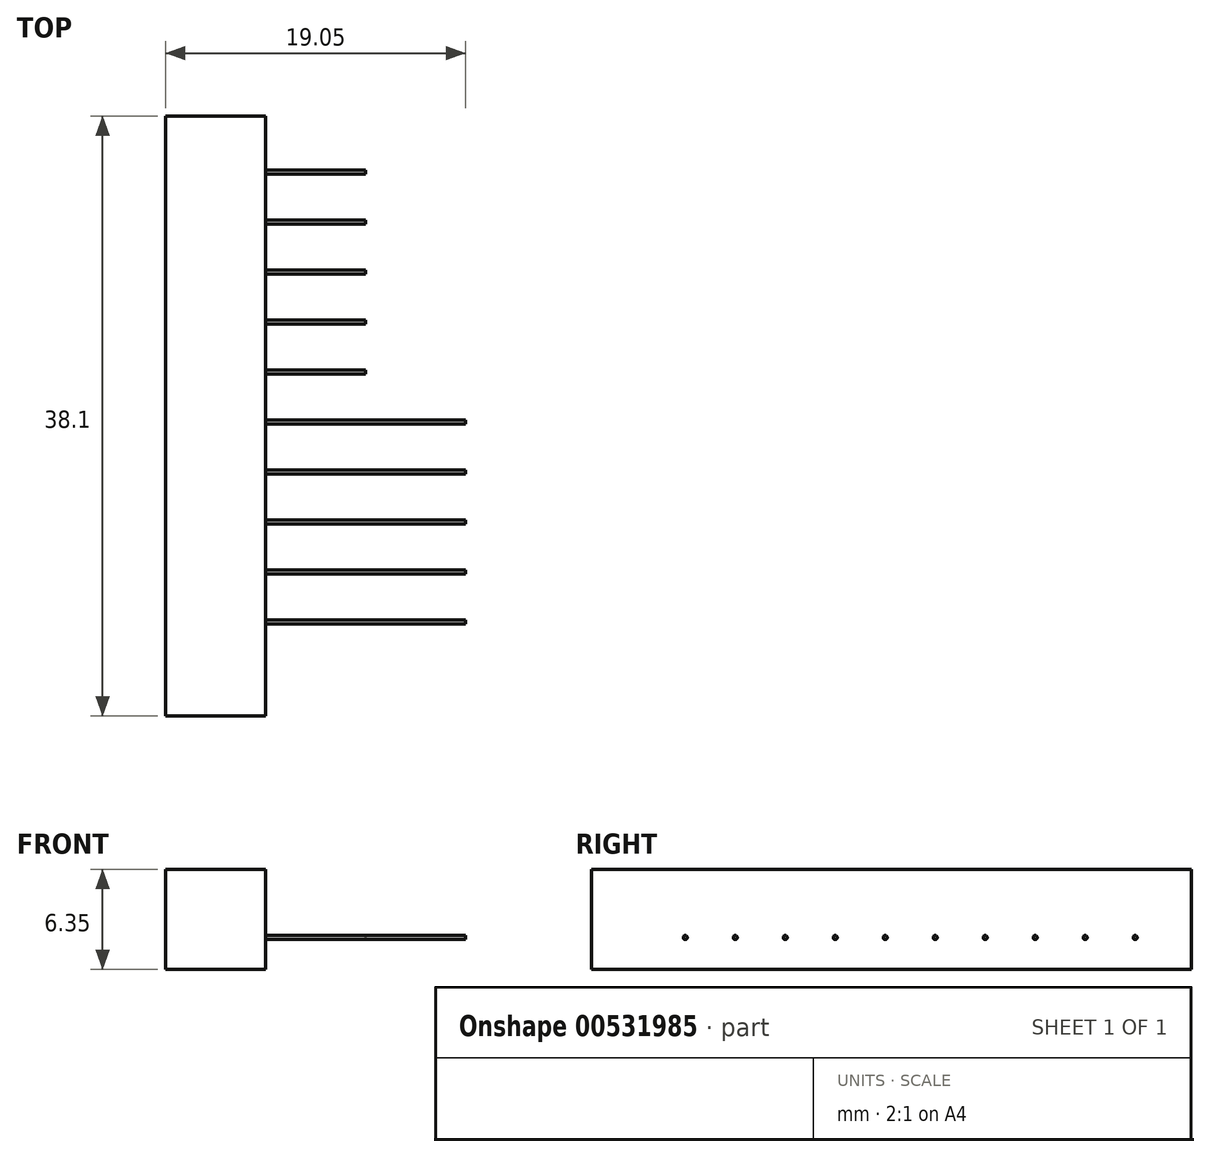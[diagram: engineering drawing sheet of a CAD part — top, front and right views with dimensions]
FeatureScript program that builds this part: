
annotation { "Feature Type Name" : "Feature", "Feature Type Description" : "" }
export const myFeature = defineFeature(function(context is Context, id is Id, definition is map)
    precondition{}
    {
        {
            var Q0;
            Q0=qCreatedBy(makeId("Top.planeOp"),FACE);
            var sketch = newSketch(context, id + "F0", { "sketchPlane" : qUnion([Q0])});
            skLineSegment(sketch, "E0.bottom", {"start": v(-14.42, 16.27) * mm, "end": v(-8.07, 16.27) * mm});
            skLineSegment(sketch, "E0.top", {"start": v(-14.42, -21.83) * mm, "end": v(-8.07, -21.83) * mm});
            skLineSegment(sketch, "E0.left", {"start": v(-14.42, 16.27) * mm, "end": v(-14.42, -21.83) * mm});
            skLineSegment(sketch, "E0.right", {"start": v(-8.07, 16.27) * mm, "end": v(-8.07, -21.83) * mm});
            skSolve(sketch);
        }
        {
            var Q0;
            Q0=makeQuery(id+"F0.imprint","IMPRINT",FACE,{"disambiguationData":[TD([[makeQuery(id+"F0.imprint","IMPRINT",EDGE,{"derivedFrom":sQuery(id+"F0.wireOp",EDGE,"E0.bottom")}),-1.0]])]});
            extrude(context, id + "F1", {"entities" : qUnion([Q0]), "depth" : 6.35 * mm, "offsetDistance" : 25.4 * mm});
        }
        {
            var Q0;
            Q0=makeQuery(id+"F1.opExtrude","SWEPT_FACE",FACE,{"disambiguationData":[OSD([sQuery(id+"F0.wireOp",EDGE,"E0.right")])]});
            var sketch = newSketch(context, id + "F2", { "sketchPlane" : qUnion([Q0])});
            skCircle(sketch, "E1", {"center": v(12.7, 2.03) * mm, "radius": 0.13 * mm});
            skCircle(sketch, "E2.1.0.0", {"center": v(9.53, 2.03) * mm, "radius": 0.13 * mm});
            skCircle(sketch, "E2.2.0.0", {"center": v(6.35, 2.03) * mm, "radius": 0.13 * mm});
            skLineSegment(sketch, "E2.direction1", {"start": v(12.7, 2.03) * mm, "end": v(9.53, 2.03) * mm, "construction": true});
            skCircle(sketch, "E3.0.3.0", {"center": v(3.17, 2.03) * mm, "radius": 0.13 * mm});
            skCircle(sketch, "E3.0.4.0", {"center": v(0, 2.03) * mm, "radius": 0.13 * mm});
            skCircle(sketch, "E3.0.5.0", {"center": v(-3.18, 2.03) * mm, "radius": 0.13 * mm});
            skCircle(sketch, "E3.0.6.0", {"center": v(-6.35, 2.03) * mm, "radius": 0.13 * mm});
            skCircle(sketch, "E3.0.7.0", {"center": v(-9.53, 2.03) * mm, "radius": 0.13 * mm});
            skCircle(sketch, "E4.0.8.0", {"center": v(-12.7, 2.03) * mm, "radius": 0.13 * mm});
            skCircle(sketch, "E4.0.9.0", {"center": v(-15.88, 2.03) * mm, "radius": 0.13 * mm});
            skSolve(sketch);
        }
        {
            var Q0;
            Q0=makeQuery(id+"F2.imprint","IMPRINT",FACE,{"disambiguationData":[TD([[makeQuery(id+"F2.imprint","IMPRINT",EDGE,{"derivedFrom":sQuery(id+"F2.wireOp",EDGE,"E3.0.5.0")}),1.0]])]});
            var Q1;
            Q1=makeQuery(id+"F2.imprint","IMPRINT",FACE,{"disambiguationData":[TD([[makeQuery(id+"F2.imprint","IMPRINT",EDGE,{"derivedFrom":sQuery(id+"F2.wireOp",EDGE,"E3.0.6.0")}),1.0]])]});
            var Q2;
            Q2=makeQuery(id+"F2.imprint","IMPRINT",FACE,{"disambiguationData":[TD([[makeQuery(id+"F2.imprint","IMPRINT",EDGE,{"derivedFrom":sQuery(id+"F2.wireOp",EDGE,"E3.0.7.0")}),1.0]])]});
            var Q3;
            Q3=makeQuery(id+"F2.imprint","IMPRINT",FACE,{"disambiguationData":[TD([[makeQuery(id+"F2.imprint","IMPRINT",EDGE,{"derivedFrom":sQuery(id+"F2.wireOp",EDGE,"E4.0.8.0")}),1.0]])]});
            var Q4;
            Q4=makeQuery(id+"F2.imprint","IMPRINT",FACE,{"disambiguationData":[TD([[makeQuery(id+"F2.imprint","IMPRINT",EDGE,{"derivedFrom":sQuery(id+"F2.wireOp",EDGE,"E4.0.9.0")}),1.0]])]});
            extrude(context, id + "F3", {"entities" : qUnion([Q0, Q1, Q2, Q3, Q4]), "operationType" : NewBodyOperationType.ADD, "depth" : 12.7 * mm, "offsetDistance" : 25.4 * mm});
        }
        {
            var Q0;
            Q0=makeQuery(id+"F2.imprint","IMPRINT",FACE,{"disambiguationData":[TD([[makeQuery(id+"F2.imprint","IMPRINT",EDGE,{"derivedFrom":sQuery(id+"F2.wireOp",EDGE,"E1")}),1.0]])]});
            var Q1;
            Q1=makeQuery(id+"F2.imprint","IMPRINT",FACE,{"disambiguationData":[TD([[makeQuery(id+"F2.imprint","IMPRINT",EDGE,{"derivedFrom":sQuery(id+"F2.wireOp",EDGE,"E2.1.0.0")}),1.0]])]});
            var Q2;
            Q2=makeQuery(id+"F2.imprint","IMPRINT",FACE,{"disambiguationData":[TD([[makeQuery(id+"F2.imprint","IMPRINT",EDGE,{"derivedFrom":sQuery(id+"F2.wireOp",EDGE,"E2.2.0.0")}),1.0]])]});
            var Q3;
            Q3=makeQuery(id+"F2.imprint","IMPRINT",FACE,{"disambiguationData":[TD([[makeQuery(id+"F2.imprint","IMPRINT",EDGE,{"derivedFrom":sQuery(id+"F2.wireOp",EDGE,"E3.0.3.0")}),1.0]])]});
            var Q4;
            Q4=makeQuery(id+"F2.imprint","IMPRINT",FACE,{"disambiguationData":[TD([[makeQuery(id+"F2.imprint","IMPRINT",EDGE,{"derivedFrom":sQuery(id+"F2.wireOp",EDGE,"E3.0.4.0")}),1.0]])]});
            extrude(context, id + "F4", {"entities" : qUnion([Q0, Q1, Q2, Q3, Q4]), "operationType" : NewBodyOperationType.ADD, "depth" : 6.35 * mm, "offsetDistance" : 25.4 * mm});
        }
    });
